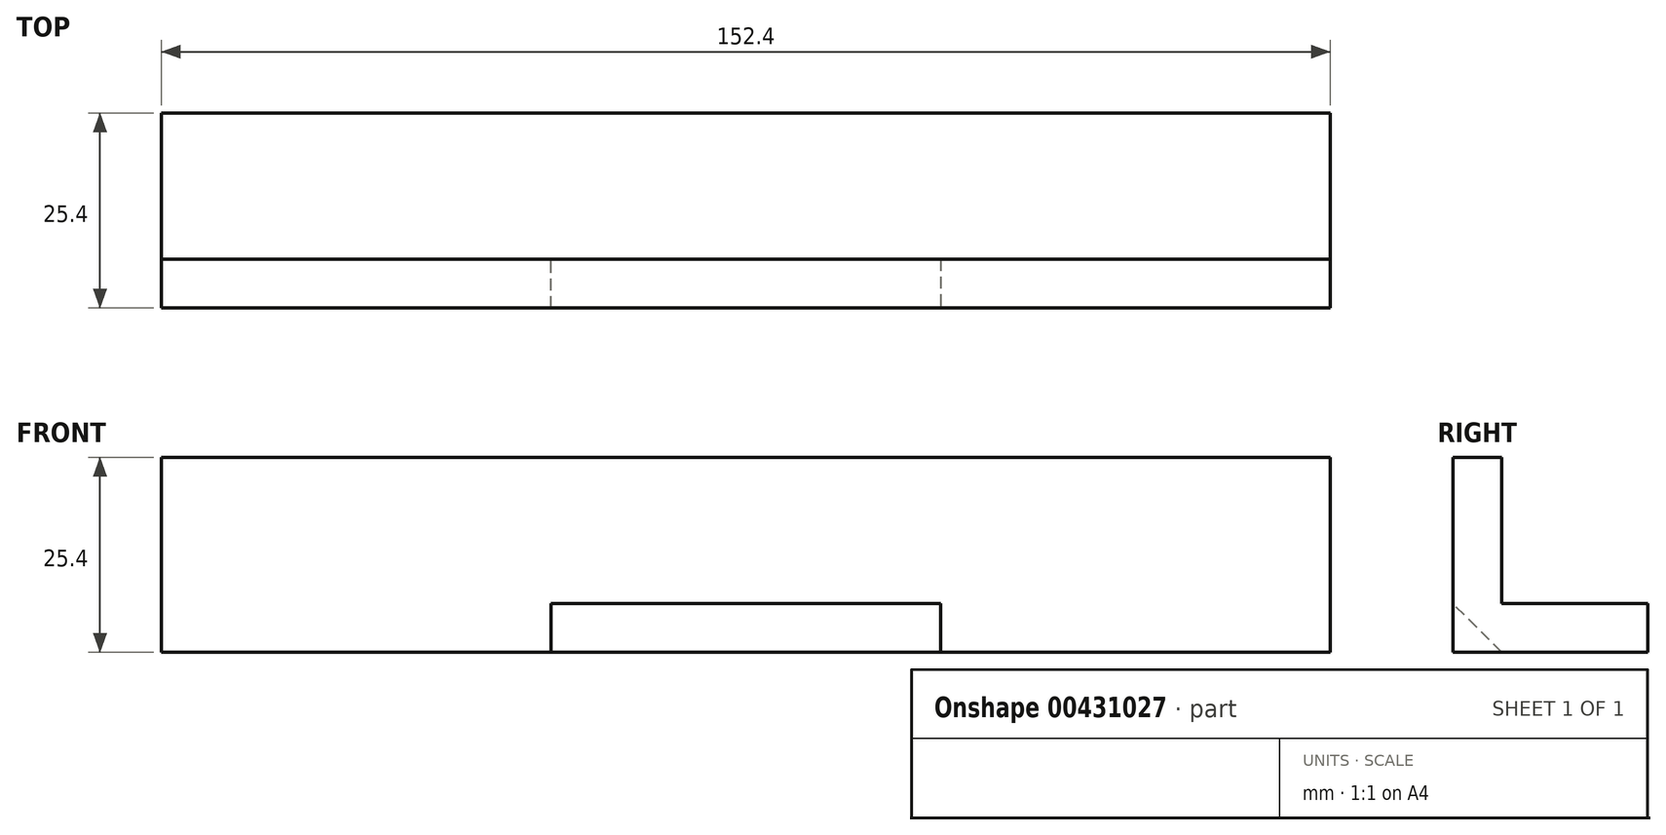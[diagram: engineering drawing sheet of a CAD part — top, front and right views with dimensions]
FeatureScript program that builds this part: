
annotation { "Feature Type Name" : "Feature", "Feature Type Description" : "" }
export const myFeature = defineFeature(function(context is Context, id is Id, definition is map)
    precondition{}
    {
        {
            var Q0;
            Q0=qCreatedBy(makeId("Right.planeOp"),FACE);
            var sketch = newSketch(context, id + "F0", { "sketchPlane" : qUnion([Q0])});
            skLineSegment(sketch, "E0", {"start": v(-16.52, 0.48) * mm, "end": v(-16.52, -24.92) * mm});
            skLineSegment(sketch, "E1", {"start": v(-16.52, -24.92) * mm, "end": v(8.88, -24.92) * mm});
            skLineSegment(sketch, "E2", {"start": v(8.88, -24.92) * mm, "end": v(8.88, -18.57) * mm});
            skLineSegment(sketch, "E3", {"start": v(8.88, -18.57) * mm, "end": v(-10.17, -18.57) * mm});
            skLineSegment(sketch, "E4", {"start": v(-10.17, -18.57) * mm, "end": v(-10.17, 0.48) * mm});
            skLineSegment(sketch, "E5", {"start": v(-10.17, 0.48) * mm, "end": v(-16.52, 0.48) * mm});
            skSolve(sketch);
        }
        {
            var Q0;
            Q0=makeQuery(id+"F0.imprint","IMPRINT",FACE,{"disambiguationData":[TD([[makeQuery(id+"F0.imprint","IMPRINT",EDGE,{"derivedFrom":sQuery(id+"F0.wireOp",EDGE,"E0")}),1.0]])]});
            extrude(context, id + "F1", {"entities" : qUnion([Q0]), "depth" : 152.4 * mm});
        }
        {
            var Q0;
            Q0=makeQuery(id+"F1.opExtrude","CAP_FACE",FACE,{"disambiguationData":[OSD([sQuery(id+"F0.wireOp",EDGE,"E0"),sQuery(id+"F0.wireOp",EDGE,"E1"),sQuery(id+"F0.wireOp",EDGE,"E2"),sQuery(id+"F0.wireOp",EDGE,"E3"),sQuery(id+"F0.wireOp",EDGE,"E4"),sQuery(id+"F0.wireOp",EDGE,"E5")])],"isStart":true});
            var sketch = newSketch(context, id + "F2", { "sketchPlane" : qUnion([Q0])});
            skLineSegment(sketch, "E6", {"start": v(16.52, -24.92) * mm, "end": v(16.52, -18.57) * mm});
            skLineSegment(sketch, "E7", {"start": v(16.52, -24.92) * mm, "end": v(10.17, -24.92) * mm});
            skLineSegment(sketch, "E8", {"start": v(16.52, -18.57) * mm, "end": v(10.17, -24.92) * mm});
            skSolve(sketch);
        }
        {
            var Q0;
            Q0=makeQuery(id+"F2.imprint","IMPRINT",FACE,{"disambiguationData":[TD([[makeQuery(id+"F2.imprint","IMPRINT",EDGE,{"derivedFrom":sQuery(id+"F2.wireOp",EDGE,"E6")}),-1.0]])]});
            extrude(context, id + "F3", {"entities" : qUnion([Q0]), "operationType" : NewBodyOperationType.REMOVE, "oppositeDirection" : true, "depth" : 154.43 * mm});
        }
        {
            var Q0;
            Q0=makeQuery(id+"F1.opExtrude","CAP_FACE",FACE,{"disambiguationData":[OSD([sQuery(id+"F0.wireOp",EDGE,"E0"),sQuery(id+"F0.wireOp",EDGE,"E1"),sQuery(id+"F0.wireOp",EDGE,"E2"),sQuery(id+"F0.wireOp",EDGE,"E3"),sQuery(id+"F0.wireOp",EDGE,"E4"),sQuery(id+"F0.wireOp",EDGE,"E5")])],"isStart":true});
            var sketch = newSketch(context, id + "F4", { "sketchPlane" : qUnion([Q0])});
            skLineSegment(sketch, "E9", {"start": v(16.52, -18.57) * mm, "end": v(16.52, -24.92) * mm});
            skLineSegment(sketch, "E10", {"start": v(16.52, -24.92) * mm, "end": v(10.17, -24.92) * mm});
            skLineSegment(sketch, "E11", {"start": v(10.17, -24.92) * mm, "end": v(16.52, -18.57) * mm});
            skSolve(sketch);
        }
        {
            var Q0;
            Q0=makeQuery(id+"F4.imprint","IMPRINT",FACE,{"disambiguationData":[TD([[makeQuery(id+"F4.imprint","IMPRINT",EDGE,{"derivedFrom":sQuery(id+"F4.wireOp",EDGE,"E9")}),-1.0]])]});
            extrude(context, id + "F5", {"entities" : qUnion([Q0]), "operationType" : NewBodyOperationType.ADD, "oppositeDirection" : true, "depth" : 50.8 * mm});
        }
        {
            var Q0;
            Q0=makeQuery(id+"F1.opExtrude","CAP_FACE",FACE,{"disambiguationData":[OSD([sQuery(id+"F0.wireOp",EDGE,"E0"),sQuery(id+"F0.wireOp",EDGE,"E1"),sQuery(id+"F0.wireOp",EDGE,"E2"),sQuery(id+"F0.wireOp",EDGE,"E3"),sQuery(id+"F0.wireOp",EDGE,"E4"),sQuery(id+"F0.wireOp",EDGE,"E5")])],"isStart":false});
            var sketch = newSketch(context, id + "F6", { "sketchPlane" : qUnion([Q0])});
            skLineSegment(sketch, "E12", {"start": v(-10.17, -24.92) * mm, "end": v(-16.52, -24.92) * mm});
            skLineSegment(sketch, "E13", {"start": v(-16.52, -24.92) * mm, "end": v(-16.52, -18.57) * mm});
            skLineSegment(sketch, "E14", {"start": v(-16.52, -18.57) * mm, "end": v(-10.17, -24.92) * mm});
            skSolve(sketch);
        }
        {
            var Q0;
            Q0=makeQuery(id+"F6.imprint","IMPRINT",FACE,{"disambiguationData":[TD([[makeQuery(id+"F6.imprint","IMPRINT",EDGE,{"derivedFrom":sQuery(id+"F6.wireOp",EDGE,"E12")}),-1.0]])]});
            extrude(context, id + "F7", {"entities" : qUnion([Q0]), "operationType" : NewBodyOperationType.ADD, "oppositeDirection" : true, "depth" : 50.8 * mm});
        }
    });
